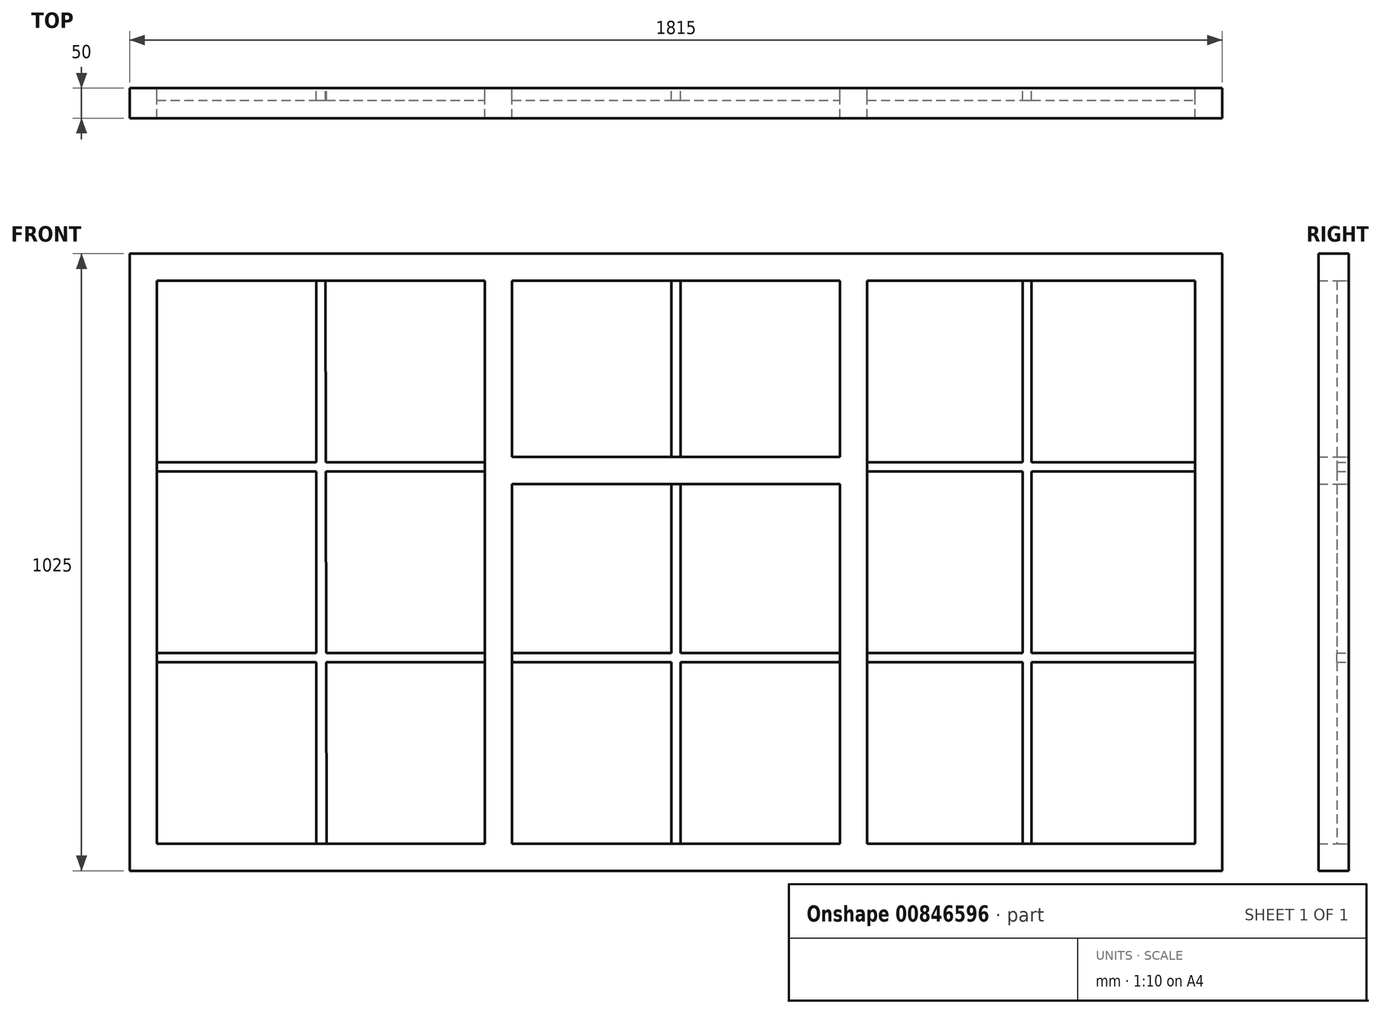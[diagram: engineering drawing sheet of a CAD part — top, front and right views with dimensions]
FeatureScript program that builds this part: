
annotation { "Feature Type Name" : "Feature", "Feature Type Description" : "" }
export const myFeature = defineFeature(function(context is Context, id is Id, definition is map)
    precondition{}
    {
        {
            var Q0;
            Q0=qCreatedBy(makeId("Front.planeOp"),FACE);
            var sketch = newSketch(context, id + "F0", { "sketchPlane" : qUnion([Q0])});
            skLineSegment(sketch, "E0.bottom", {"start": v(0, 0) * mm, "end": v(1815, 0) * mm});
            skLineSegment(sketch, "E0.top", {"start": v(0, 1025) * mm, "end": v(1815, 1025) * mm});
            skLineSegment(sketch, "E0.left", {"start": v(0, 0) * mm, "end": v(0, 1025) * mm});
            skLineSegment(sketch, "E0.right", {"start": v(1815, 0) * mm, "end": v(1815, 1025) * mm});
            skLineSegment(sketch, "E1.bottom", {"start": v(45, 980) * mm, "end": v(590, 980) * mm});
            skLineSegment(sketch, "E1.top", {"start": v(45, 45) * mm, "end": v(590, 45) * mm});
            skLineSegment(sketch, "E1.left", {"start": v(45, 980) * mm, "end": v(45, 45) * mm});
            skLineSegment(sketch, "E1.right", {"start": v(590, 980) * mm, "end": v(590, 45) * mm});
            skLineSegment(sketch, "E2.bottom", {"start": v(635, 980) * mm, "end": v(1180, 980) * mm});
            skLineSegment(sketch, "E2.top", {"start": v(635, 687.5) * mm, "end": v(1180, 687.5) * mm});
            skLineSegment(sketch, "E2.left", {"start": v(635, 980) * mm, "end": v(635, 687.5) * mm});
            skLineSegment(sketch, "E2.right", {"start": v(1180, 980) * mm, "end": v(1180, 687.5) * mm});
            skLineSegment(sketch, "E3.bottom", {"start": v(635, 642.5) * mm, "end": v(1180, 642.5) * mm});
            skLineSegment(sketch, "E3.top", {"start": v(635, 45) * mm, "end": v(1180, 45) * mm});
            skLineSegment(sketch, "E3.left", {"start": v(635, 642.5) * mm, "end": v(635, 45) * mm});
            skLineSegment(sketch, "E3.right", {"start": v(1180, 642.5) * mm, "end": v(1180, 45) * mm});
            skLineSegment(sketch, "E4.bottom", {"start": v(1225, 980) * mm, "end": v(1770, 980) * mm});
            skLineSegment(sketch, "E4.top", {"start": v(1225, 45) * mm, "end": v(1770, 45) * mm});
            skLineSegment(sketch, "E4.left", {"start": v(1225, 980) * mm, "end": v(1225, 45) * mm});
            skLineSegment(sketch, "E4.right", {"start": v(1770, 980) * mm, "end": v(1770, 45) * mm});
            skSolve(sketch);
        }
        {
            var Q0;
            Q0=qSketchRegion(id+"F0",true);
            extrude(context, id + "F1", {"entities" : qUnion([Q0]), "depth" : 50 * mm, "offsetDistance" : 25 * mm});
        }
        {
            var Q0;
            Q0=qCreatedBy(makeId("Front.planeOp"),FACE);
            var sketch = newSketch(context, id + "F2", { "sketchPlane" : qUnion([Q0])});
            skLineSegment(sketch, "E5.bottom", {"start": v(310, 980) * mm, "end": v(325, 980) * mm});
            skLineSegment(sketch, "E5.top", {"start": v(310, 45) * mm, "end": v(327.01, 45) * mm});
            skLineSegment(sketch, "E6.bottom", {"start": v(45, 678.33) * mm, "end": v(310, 678.33) * mm});
            skLineSegment(sketch, "E6.top", {"start": v(45, 663.33) * mm, "end": v(310, 663.33) * mm});
            skLineSegment(sketch, "E6.left", {"start": v(45, 678.33) * mm, "end": v(45, 663.33) * mm});
            skLineSegment(sketch, "E6.right", {"start": v(590, 678.33) * mm, "end": v(590, 663.33) * mm});
            skLineSegment(sketch, "E7.bottom", {"start": v(45, 361.67) * mm, "end": v(310, 361.67) * mm});
            skLineSegment(sketch, "E7.top", {"start": v(45, 346.67) * mm, "end": v(310, 346.67) * mm});
            skLineSegment(sketch, "E7.left", {"start": v(45, 361.67) * mm, "end": v(45, 346.67) * mm});
            skLineSegment(sketch, "E7.right", {"start": v(590, 361.67) * mm, "end": v(590, 346.67) * mm});
            skLineSegment(sketch, "E8.trimOffspring", {"start": v(325, 980) * mm, "end": v(325.65, 678.33) * mm});
            skLineSegment(sketch, "E9.trimOffspring", {"start": v(310, 980) * mm, "end": v(310, 678.33) * mm});
            skLineSegment(sketch, "E10.trimOffspring", {"start": v(325.65, 678.33) * mm, "end": v(590, 678.33) * mm});
            skLineSegment(sketch, "E11.trimOffspring", {"start": v(310, 663.33) * mm, "end": v(310, 361.67) * mm});
            skLineSegment(sketch, "E12.trimOffspring", {"start": v(325.68, 663.33) * mm, "end": v(590, 663.33) * mm});
            skLineSegment(sketch, "E13.trimOffspring", {"start": v(325.68, 663.33) * mm, "end": v(326.33, 361.67) * mm});
            skLineSegment(sketch, "E14.trimOffspring", {"start": v(326.33, 361.67) * mm, "end": v(590, 361.67) * mm});
            skLineSegment(sketch, "E15.trimOffspring", {"start": v(310, 346.67) * mm, "end": v(310, 45) * mm});
            skLineSegment(sketch, "E16.trimOffspring", {"start": v(326.36, 346.67) * mm, "end": v(590, 346.67) * mm});
            skLineSegment(sketch, "E17.trimOffspring", {"start": v(326.36, 346.67) * mm, "end": v(327.01, 45) * mm});
            skLineSegment(sketch, "E18.bottom", {"start": v(1483.1, 980) * mm, "end": v(1498.1, 980) * mm});
            skLineSegment(sketch, "E18.top", {"start": v(1483.1, 45) * mm, "end": v(1498.1, 45) * mm});
            skLineSegment(sketch, "E18.left", {"start": v(1483.1, 980) * mm, "end": v(1483.1, 678.33) * mm});
            skLineSegment(sketch, "E18.right", {"start": v(1498.1, 980) * mm, "end": v(1498.1, 678.33) * mm});
            skLineSegment(sketch, "E19.bottom", {"start": v(1225, 678.33) * mm, "end": v(1483.1, 678.33) * mm});
            skLineSegment(sketch, "E19.top", {"start": v(1225, 663.33) * mm, "end": v(1483.1, 663.33) * mm});
            skLineSegment(sketch, "E19.left", {"start": v(1225, 678.33) * mm, "end": v(1225, 663.33) * mm});
            skLineSegment(sketch, "E19.right", {"start": v(1770, 678.33) * mm, "end": v(1770, 663.33) * mm});
            skLineSegment(sketch, "E20.bottom", {"start": v(1225, 346.67) * mm, "end": v(1483.1, 346.67) * mm});
            skLineSegment(sketch, "E20.top", {"start": v(1225, 361.67) * mm, "end": v(1483.1, 361.67) * mm});
            skLineSegment(sketch, "E20.left", {"start": v(1225, 346.67) * mm, "end": v(1225, 361.67) * mm});
            skLineSegment(sketch, "E20.right", {"start": v(1770, 346.67) * mm, "end": v(1770, 361.67) * mm});
            skLineSegment(sketch, "E21.trimOffspring", {"start": v(1483.1, 663.33) * mm, "end": v(1483.1, 361.67) * mm});
            skLineSegment(sketch, "E22.trimOffspring", {"start": v(1498.1, 678.33) * mm, "end": v(1770, 678.33) * mm});
            skLineSegment(sketch, "E23.trimOffspring", {"start": v(1498.1, 663.33) * mm, "end": v(1498.1, 361.67) * mm});
            skLineSegment(sketch, "E24.trimOffspring", {"start": v(1498.1, 663.33) * mm, "end": v(1770, 663.33) * mm});
            skLineSegment(sketch, "E25.trimOffspring", {"start": v(1498.1, 361.67) * mm, "end": v(1770, 361.67) * mm});
            skLineSegment(sketch, "E26.trimOffspring", {"start": v(1483.1, 346.67) * mm, "end": v(1483.1, 45) * mm});
            skLineSegment(sketch, "E27.trimOffspring", {"start": v(1498.1, 346.67) * mm, "end": v(1770, 346.67) * mm});
            skLineSegment(sketch, "E28.trimOffspring", {"start": v(1498.1, 346.67) * mm, "end": v(1498.1, 45) * mm});
            skLineSegment(sketch, "E29.bottom", {"start": v(900, 980) * mm, "end": v(915, 980) * mm});
            skLineSegment(sketch, "E29.top", {"start": v(900, 687.5) * mm, "end": v(915, 687.5) * mm});
            skLineSegment(sketch, "E29.left", {"start": v(900, 980) * mm, "end": v(900, 687.5) * mm});
            skLineSegment(sketch, "E29.right", {"start": v(915, 980) * mm, "end": v(915, 687.5) * mm});
            skLineSegment(sketch, "E30.bottom", {"start": v(900, 642.5) * mm, "end": v(915, 642.5) * mm});
            skLineSegment(sketch, "E30.top", {"start": v(900, 45) * mm, "end": v(915, 45) * mm});
            skLineSegment(sketch, "E30.left", {"start": v(900, 642.5) * mm, "end": v(900, 361.67) * mm});
            skLineSegment(sketch, "E30.right", {"start": v(915, 642.5) * mm, "end": v(915, 361.67) * mm});
            skLineSegment(sketch, "E31.bottom", {"start": v(635, 361.67) * mm, "end": v(900, 361.67) * mm});
            skLineSegment(sketch, "E31.top", {"start": v(635, 346.67) * mm, "end": v(900, 346.67) * mm});
            skLineSegment(sketch, "E31.left", {"start": v(635, 361.67) * mm, "end": v(635, 346.67) * mm});
            skLineSegment(sketch, "E31.right", {"start": v(1180, 361.67) * mm, "end": v(1180, 346.67) * mm});
            skLineSegment(sketch, "E32.trimOffspring", {"start": v(915, 361.67) * mm, "end": v(1180, 361.67) * mm});
            skLineSegment(sketch, "E33.trimOffspring", {"start": v(900, 346.67) * mm, "end": v(900, 45) * mm});
            skLineSegment(sketch, "E34.trimOffspring", {"start": v(915, 346.67) * mm, "end": v(1180, 346.67) * mm});
            skLineSegment(sketch, "E35.trimOffspring", {"start": v(915, 346.67) * mm, "end": v(915, 45) * mm});
            skSolve(sketch);
        }
        {
            var Q0;
            Q0 = qSketchRegion(id + "F2", true);
            extrude(context, id + "F3", {"entities" : qUnion([Q0]), "operationType" : NewBodyOperationType.ADD, "depth" : 20 * mm, "offsetDistance" : 25 * mm});
        }
    });
